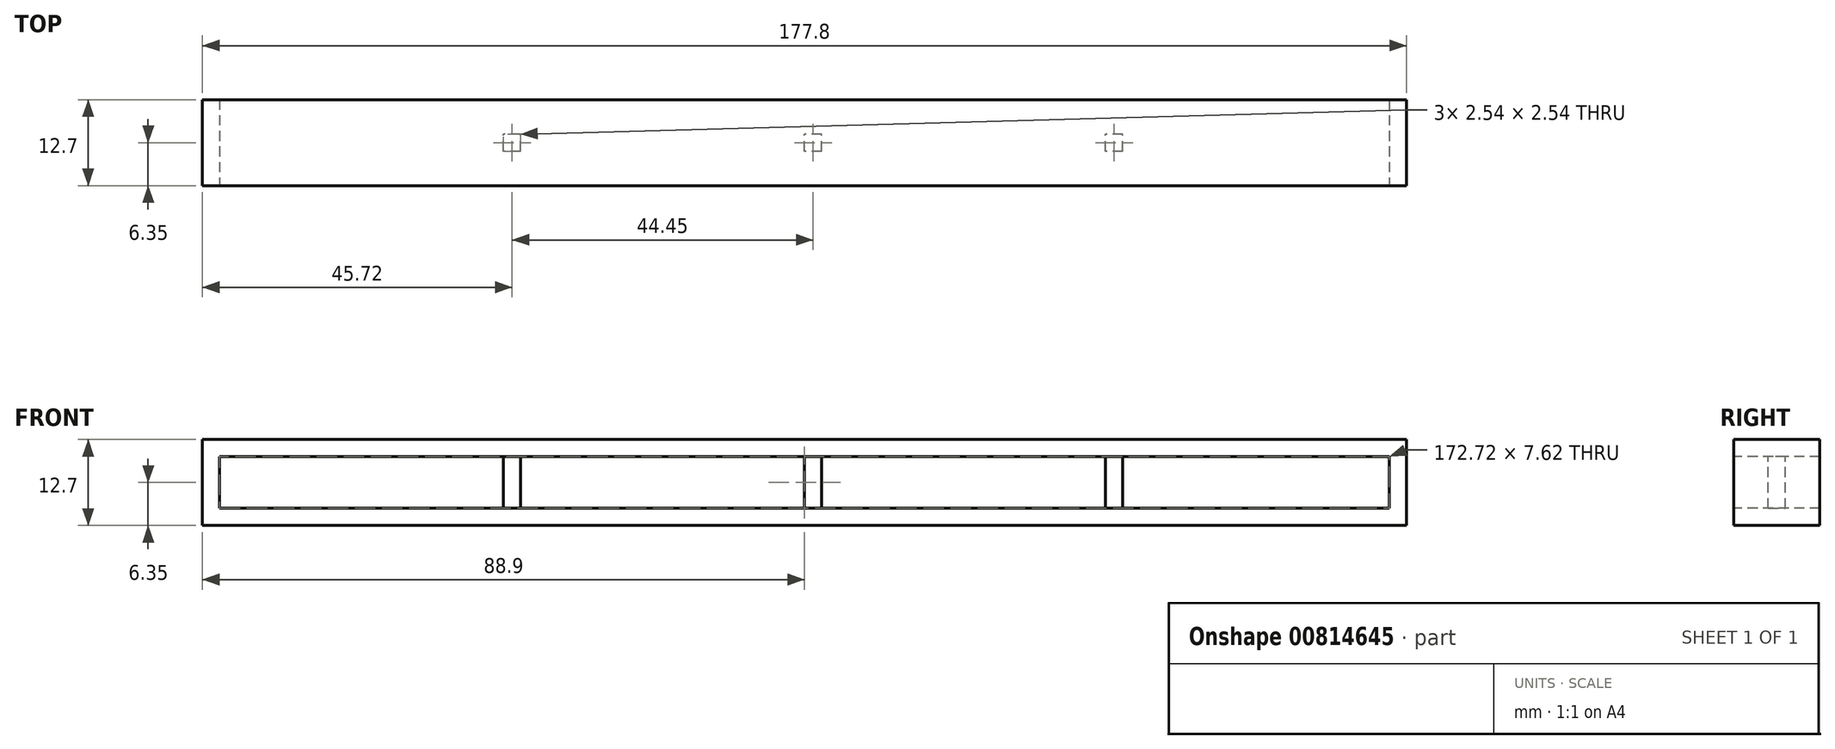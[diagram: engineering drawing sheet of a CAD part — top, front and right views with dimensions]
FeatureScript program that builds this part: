
annotation { "Feature Type Name" : "Feature", "Feature Type Description" : "" }
export const myFeature = defineFeature(function(context is Context, id is Id, definition is map)
    precondition{}
    {
        {
            var Q0;
            Q0=qCreatedBy(makeId("Right.planeOp"),FACE);
            var sketch = newSketch(context, id + "F0", { "sketchPlane" : qUnion([Q0])});
            skLineSegment(sketch, "E0.bottom", {"start": v(0, 0) * mm, "end": v(12.7, 0) * mm});
            skLineSegment(sketch, "E0.top", {"start": v(0, -2.54) * mm, "end": v(12.7, -2.54) * mm});
            skLineSegment(sketch, "E0.left", {"start": v(0, 0) * mm, "end": v(0, -2.54) * mm});
            skLineSegment(sketch, "E0.right", {"start": v(12.7, 0) * mm, "end": v(12.7, -2.54) * mm});
            skSolve(sketch);
        }
        {
            var Q0;
            Q0=qCreatedBy(makeId("Front.planeOp"),FACE);
            var sketch = newSketch(context, id + "F1", { "sketchPlane" : qUnion([Q0])});
            skLineSegment(sketch, "E1.bottom", {"start": v(0, 0) * mm, "end": v(177.8, 0) * mm});
            skLineSegment(sketch, "E1.top", {"start": v(0, -12.7) * mm, "end": v(177.8, -12.7) * mm});
            skLineSegment(sketch, "E1.left", {"start": v(0, 0) * mm, "end": v(0, -12.7) * mm});
            skLineSegment(sketch, "E1.right", {"start": v(177.8, 0) * mm, "end": v(177.8, -12.7) * mm});
            skSolve(sketch);
        }
        {
            var Q0;
            Q0=makeQuery(id+"F0.imprint","IMPRINT",FACE,{"disambiguationData":[TD([[makeQuery(id+"F0.imprint","IMPRINT",EDGE,{"derivedFrom":sQuery(id+"F0.wireOp",EDGE,"E0.bottom")}),-1.0]])]});
            var Q1;
            Q1=sQuery(id+"F1.wireOp",EDGE,"E1.bottom");
            var Q2;
            Q2=sQuery(id+"F1.wireOp",EDGE,"E1.left");
            var Q3;
            Q3=sQuery(id+"F1.wireOp",EDGE,"E1.top");
            var Q4;
            Q4=sQuery(id+"F1.wireOp",EDGE,"E1.right");
            sweep(context, id + "F2", {"profiles" : qUnion([Q0]), "path" : qUnion([Q1, Q2, Q3, Q4])});
        }
        {
            var Q0;
            Q0=makeQuery(id+"F2.opSweep","SWEPT_FACE",FACE,{"disambiguationData":[OSD([sQuery(id+"F0.wireOp",EDGE,"E0.bottom"),sQuery(id+"F1.wireOp",EDGE,"E1.bottom")])]});
            var sketch = newSketch(context, id + "F3", { "sketchPlane" : qUnion([Q0])});
            skLineSegment(sketch, "E2.bottom", {"start": v(47, 5.08) * mm, "end": v(44.45, 5.08) * mm});
            skLineSegment(sketch, "E2.top", {"start": v(47, 7.62) * mm, "end": v(44.45, 7.62) * mm});
            skLineSegment(sketch, "E2.left", {"start": v(47, 5.08) * mm, "end": v(47, 7.62) * mm});
            skLineSegment(sketch, "E2.right", {"start": v(44.45, 5.08) * mm, "end": v(44.45, 7.62) * mm});
            skPoint(sketch, "E2.middle", {"position": v(45.72, 6.35) * mm});
            skLineSegment(sketch, "E3.1.0.0", {"start": v(91.44, 7.62) * mm, "end": v(88.9, 7.62) * mm});
            skLineSegment(sketch, "E3.1.0.1", {"start": v(91.44, 5.08) * mm, "end": v(91.44, 7.62) * mm});
            skLineSegment(sketch, "E3.1.0.2", {"start": v(91.44, 5.08) * mm, "end": v(88.9, 5.08) * mm});
            skLineSegment(sketch, "E3.1.0.3", {"start": v(88.9, 5.08) * mm, "end": v(88.9, 7.62) * mm});
            skLineSegment(sketch, "E3.2.0.0", {"start": v(135.9, 7.62) * mm, "end": v(133.35, 7.62) * mm});
            skLineSegment(sketch, "E3.2.0.1", {"start": v(135.9, 5.08) * mm, "end": v(135.9, 7.62) * mm});
            skLineSegment(sketch, "E3.2.0.2", {"start": v(135.9, 5.08) * mm, "end": v(133.35, 5.08) * mm});
            skLineSegment(sketch, "E3.2.0.3", {"start": v(133.35, 5.08) * mm, "end": v(133.35, 7.62) * mm});
            skLineSegment(sketch, "E3.direction1", {"start": v(44.45, 5.08) * mm, "end": v(88.9, 5.08) * mm, "construction": true});
            skSolve(sketch);
        }
        {
            var Q0;
            Q0 = qSketchRegion(id + "F3", true);
            extrude(context, id + "F4", {"entities" : qUnion([Q0]), "operationType" : NewBodyOperationType.ADD, "oppositeDirection" : true, "depth" : 12.7 * mm, "offsetDistance" : 25.4 * mm});
        }
    });
